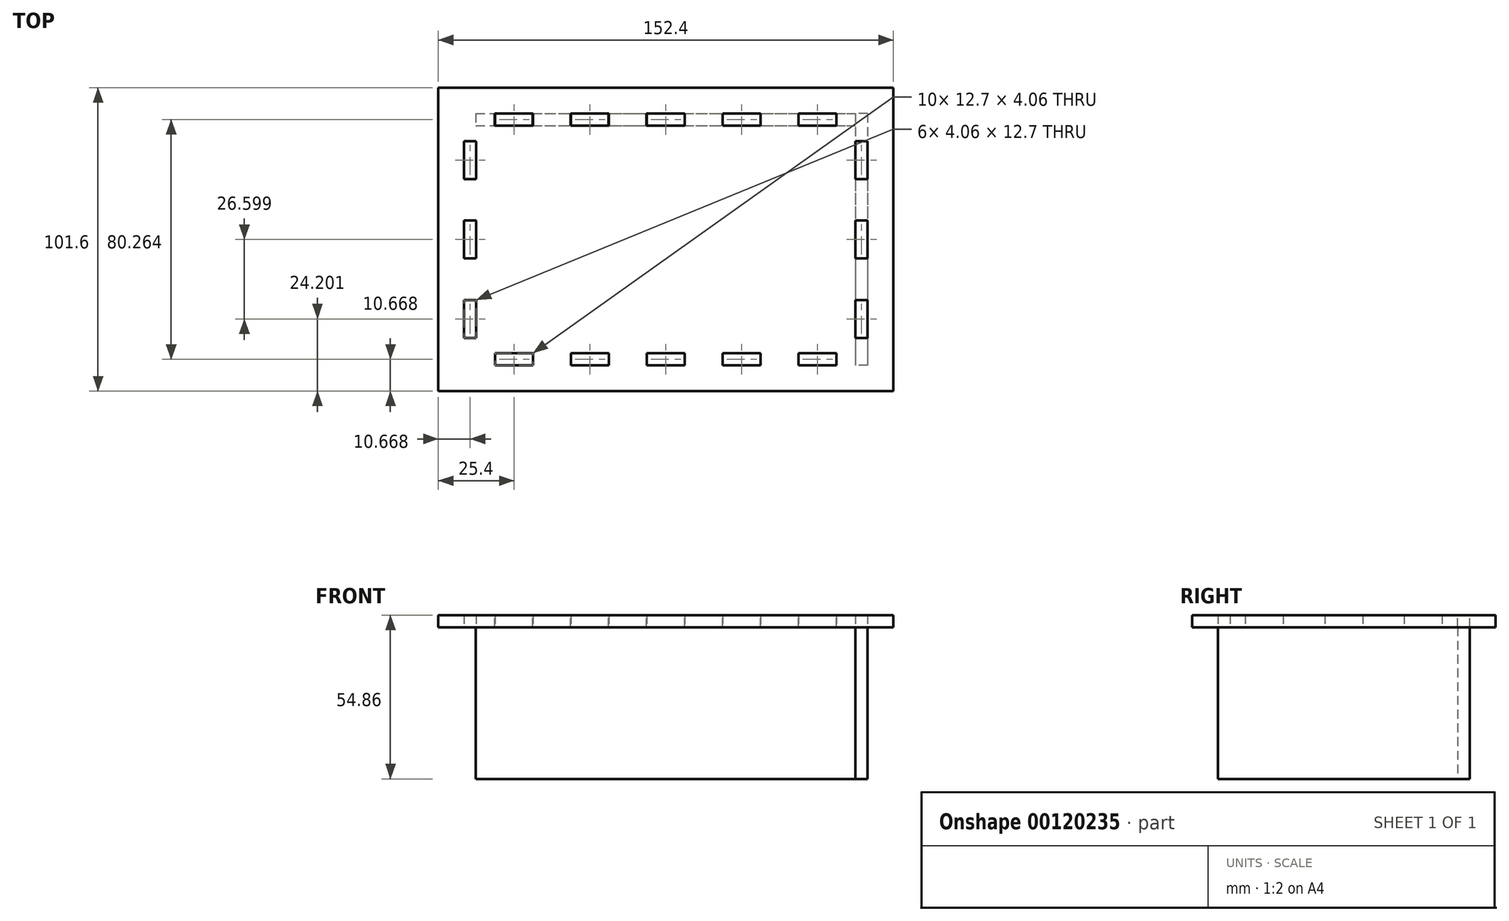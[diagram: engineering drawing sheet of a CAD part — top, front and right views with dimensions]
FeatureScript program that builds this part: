
annotation { "Feature Type Name" : "Feature", "Feature Type Description" : "" }
export const myFeature = defineFeature(function(context is Context, id is Id, definition is map)
    precondition{}
    {
        {
            assignVariable(context, id + "F0", {"name" : "T", "anyValue" : 4.06 * mm});
        }
        {
            var Q0;
            Q0=qCreatedBy(makeId("Top.planeOp"),FACE);
            var sketch = newSketch(context, id + "F1", { "sketchPlane" : qUnion([Q0])});
            skLineSegment(sketch, "E0.bottom", {"start": v(0, 0) * mm, "end": v(152.4, 0) * mm});
            skLineSegment(sketch, "E0.top", {"start": v(0, -101.6) * mm, "end": v(152.4, -101.6) * mm});
            skLineSegment(sketch, "E0.left", {"start": v(0, 0) * mm, "end": v(0, -101.6) * mm});
            skLineSegment(sketch, "E0.right", {"start": v(152.4, 0) * mm, "end": v(152.4, -101.6) * mm});
            skLineSegment(sketch, "E1.bottom", {"start": v(19.05, -8.64) * mm, "end": v(31.75, -8.64) * mm});
            skLineSegment(sketch, "E1.top", {"start": v(19.05, -12.7) * mm, "end": v(31.75, -12.7) * mm});
            skLineSegment(sketch, "E1.left", {"start": v(19.05, -8.64) * mm, "end": v(19.05, -12.7) * mm});
            skLineSegment(sketch, "E1.right", {"start": v(31.75, -8.64) * mm, "end": v(31.75, -12.7) * mm});
            skLineSegment(sketch, "E2.1.0.0", {"start": v(57.15, -8.64) * mm, "end": v(57.15, -12.7) * mm});
            skLineSegment(sketch, "E2.1.0.1", {"start": v(44.45, -8.64) * mm, "end": v(44.45, -12.7) * mm});
            skLineSegment(sketch, "E2.1.0.2", {"start": v(44.45, -12.7) * mm, "end": v(57.15, -12.7) * mm});
            skLineSegment(sketch, "E2.1.0.3", {"start": v(44.45, -8.64) * mm, "end": v(57.15, -8.64) * mm});
            skLineSegment(sketch, "E2.2.0.0", {"start": v(82.55, -8.64) * mm, "end": v(82.55, -12.7) * mm});
            skLineSegment(sketch, "E2.2.0.1", {"start": v(69.85, -8.64) * mm, "end": v(69.85, -12.7) * mm});
            skLineSegment(sketch, "E2.2.0.2", {"start": v(69.85, -12.7) * mm, "end": v(82.55, -12.7) * mm});
            skLineSegment(sketch, "E2.2.0.3", {"start": v(69.85, -8.64) * mm, "end": v(82.55, -8.64) * mm});
            skLineSegment(sketch, "E2.3.0.0", {"start": v(107.95, -8.64) * mm, "end": v(107.95, -12.7) * mm});
            skLineSegment(sketch, "E2.3.0.1", {"start": v(95.25, -8.64) * mm, "end": v(95.25, -12.7) * mm});
            skLineSegment(sketch, "E2.3.0.2", {"start": v(95.25, -12.7) * mm, "end": v(107.95, -12.7) * mm});
            skLineSegment(sketch, "E2.3.0.3", {"start": v(95.25, -8.64) * mm, "end": v(107.95, -8.64) * mm});
            skLineSegment(sketch, "E2.4.0.0", {"start": v(133.35, -8.64) * mm, "end": v(133.35, -12.7) * mm});
            skLineSegment(sketch, "E2.4.0.1", {"start": v(120.65, -8.64) * mm, "end": v(120.65, -12.7) * mm});
            skLineSegment(sketch, "E2.4.0.2", {"start": v(120.65, -12.7) * mm, "end": v(133.35, -12.7) * mm});
            skLineSegment(sketch, "E2.4.0.3", {"start": v(120.65, -8.64) * mm, "end": v(133.35, -8.64) * mm});
            skLineSegment(sketch, "E2.direction1", {"start": v(19.05, -12.7) * mm, "end": v(44.45, -12.7) * mm, "construction": true});
            skLineSegment(sketch, "E3", {"start": v(0, -50.8) * mm, "end": v(152.4, -50.8) * mm, "construction": true});
            skLineSegment(sketch, "E4.MirrorCS", {"start": v(19.05, -88.9) * mm, "end": v(31.75, -88.9) * mm});
            skLineSegment(sketch, "E5.MirrorCS", {"start": v(19.05, -88.9) * mm, "end": v(44.45, -88.9) * mm, "construction": true});
            skLineSegment(sketch, "E6.MirrorCS", {"start": v(95.25, -92.96) * mm, "end": v(107.95, -92.96) * mm});
            skLineSegment(sketch, "E7.MirrorCS", {"start": v(120.65, -92.96) * mm, "end": v(120.65, -88.9) * mm});
            skLineSegment(sketch, "E8.MirrorCS", {"start": v(69.85, -92.96) * mm, "end": v(69.85, -88.9) * mm});
            skLineSegment(sketch, "E9.MirrorCS", {"start": v(95.25, -92.96) * mm, "end": v(95.25, -88.9) * mm});
            skLineSegment(sketch, "E10.MirrorCS", {"start": v(69.85, -88.9) * mm, "end": v(82.55, -88.9) * mm});
            skLineSegment(sketch, "E11.MirrorCS", {"start": v(69.85, -92.96) * mm, "end": v(82.55, -92.96) * mm});
            skLineSegment(sketch, "E12.MirrorCS", {"start": v(120.65, -88.9) * mm, "end": v(133.35, -88.9) * mm});
            skLineSegment(sketch, "E13.MirrorCS", {"start": v(95.25, -88.9) * mm, "end": v(107.95, -88.9) * mm});
            skLineSegment(sketch, "E14.MirrorCS", {"start": v(19.05, -92.96) * mm, "end": v(31.75, -92.96) * mm});
            skLineSegment(sketch, "E15.MirrorCS", {"start": v(19.05, -92.96) * mm, "end": v(19.05, -88.9) * mm});
            skLineSegment(sketch, "E16.MirrorCS", {"start": v(133.35, -92.96) * mm, "end": v(133.35, -88.9) * mm});
            skLineSegment(sketch, "E17.MirrorCS", {"start": v(31.75, -92.96) * mm, "end": v(31.75, -88.9) * mm});
            skLineSegment(sketch, "E18.MirrorCS", {"start": v(107.95, -92.96) * mm, "end": v(107.95, -88.9) * mm});
            skLineSegment(sketch, "E19.MirrorCS", {"start": v(57.15, -92.96) * mm, "end": v(57.15, -88.9) * mm});
            skLineSegment(sketch, "E20.MirrorCS", {"start": v(44.45, -92.96) * mm, "end": v(44.45, -88.9) * mm});
            skLineSegment(sketch, "E21.MirrorCS", {"start": v(44.45, -88.9) * mm, "end": v(57.15, -88.9) * mm});
            skLineSegment(sketch, "E22.MirrorCS", {"start": v(44.45, -92.96) * mm, "end": v(57.15, -92.96) * mm});
            skLineSegment(sketch, "E23.MirrorCS", {"start": v(82.55, -92.96) * mm, "end": v(82.55, -88.9) * mm});
            skLineSegment(sketch, "E24.MirrorCS", {"start": v(120.65, -92.96) * mm, "end": v(133.35, -92.96) * mm});
            skLineSegment(sketch, "E25.bottom", {"start": v(139.7, -17.85) * mm, "end": v(143.76, -17.85) * mm});
            skLineSegment(sketch, "E25.top", {"start": v(139.7, -30.55) * mm, "end": v(143.76, -30.55) * mm});
            skLineSegment(sketch, "E25.left", {"start": v(139.7, -17.85) * mm, "end": v(139.7, -30.55) * mm});
            skLineSegment(sketch, "E25.right", {"start": v(143.76, -17.85) * mm, "end": v(143.76, -30.55) * mm});
            skLineSegment(sketch, "E26.1.0.0", {"start": v(143.76, -44.45) * mm, "end": v(143.76, -57.15) * mm});
            skLineSegment(sketch, "E26.1.0.1", {"start": v(139.7, -44.45) * mm, "end": v(139.7, -57.15) * mm});
            skLineSegment(sketch, "E26.1.0.2", {"start": v(139.7, -44.45) * mm, "end": v(143.76, -44.45) * mm});
            skLineSegment(sketch, "E26.1.0.3", {"start": v(139.7, -57.15) * mm, "end": v(143.76, -57.15) * mm});
            skLineSegment(sketch, "E26.2.0.0", {"start": v(143.76, -71.05) * mm, "end": v(143.76, -83.75) * mm});
            skLineSegment(sketch, "E26.2.0.1", {"start": v(139.7, -71.05) * mm, "end": v(139.7, -83.75) * mm});
            skLineSegment(sketch, "E26.2.0.2", {"start": v(139.7, -71.05) * mm, "end": v(143.76, -71.05) * mm});
            skLineSegment(sketch, "E26.2.0.3", {"start": v(139.7, -83.75) * mm, "end": v(143.76, -83.75) * mm});
            skLineSegment(sketch, "E26.direction1", {"start": v(139.7, -30.55) * mm, "end": v(139.7, -57.15) * mm, "construction": true});
            skPoint(sketch, "E27", {"position": v(143.76, -50.8) * mm});
            skLineSegment(sketch, "E28", {"start": v(76.2, 0) * mm, "end": v(76.2, -101.6) * mm, "construction": true});
            skLineSegment(sketch, "E29.MirrorCS", {"start": v(12.7, -44.45) * mm, "end": v(12.7, -57.15) * mm});
            skLineSegment(sketch, "E30.MirrorCS", {"start": v(12.7, -17.85) * mm, "end": v(8.64, -17.85) * mm});
            skLineSegment(sketch, "E31.MirrorCS", {"start": v(12.7, -57.15) * mm, "end": v(8.64, -57.15) * mm});
            skLineSegment(sketch, "E32.MirrorCS", {"start": v(12.7, -71.05) * mm, "end": v(8.64, -71.05) * mm});
            skLineSegment(sketch, "E33.MirrorCS", {"start": v(12.7, -71.05) * mm, "end": v(12.7, -83.75) * mm});
            skLineSegment(sketch, "E34.MirrorCS", {"start": v(12.7, -44.45) * mm, "end": v(8.64, -44.45) * mm});
            skLineSegment(sketch, "E35.MirrorCS", {"start": v(12.7, -30.55) * mm, "end": v(12.7, -57.15) * mm, "construction": true});
            skLineSegment(sketch, "E36.MirrorCS", {"start": v(8.64, -71.05) * mm, "end": v(8.64, -83.75) * mm});
            skLineSegment(sketch, "E37.MirrorCS", {"start": v(12.7, -17.85) * mm, "end": v(12.7, -30.55) * mm});
            skPoint(sketch, "E38.MirrorP", {"position": v(8.64, -50.8) * mm});
            skLineSegment(sketch, "E39.MirrorCS", {"start": v(8.64, -44.45) * mm, "end": v(8.64, -57.15) * mm});
            skLineSegment(sketch, "E40.MirrorCS", {"start": v(12.7, -30.55) * mm, "end": v(8.64, -30.55) * mm});
            skLineSegment(sketch, "E41.MirrorCS", {"start": v(8.64, -17.85) * mm, "end": v(8.64, -30.55) * mm});
            skLineSegment(sketch, "E42.MirrorCS", {"start": v(12.7, -83.75) * mm, "end": v(8.64, -83.75) * mm});
            skSolve(sketch);
        }
        {
            var Q0;
            Q0=makeQuery(id+"F1.imprint","IMPRINT",FACE,{"disambiguationData":[TD([[makeQuery(id+"F1.imprint","IMPRINT",EDGE,{"derivedFrom":sQuery(id+"F1.wireOp",EDGE,"E0.bottom")}),-1.0]])]});
            extrude(context, id + "F2", {"entities" : qUnion([Q0]), "depth" : getVariable(context, 'T')});
        }
        {
            var Q0;
            Q0=makeQuery(id+"F2.opExtrude","SWEPT_FACE",FACE,{"disambiguationData":[OSD([sQuery(id+"F1.wireOp",EDGE,"E2.2.0.2")])]});
            var sketch = newSketch(context, id + "F3", { "sketchPlane" : qUnion([Q0])});
            skLineSegment(sketch, "E43.bottom", {"start": v(-12.6, 0) * mm, "end": v(-139.6, 0) * mm});
            skLineSegment(sketch, "E43.top", {"start": v(-12.6, -50.8) * mm, "end": v(-139.6, -50.8) * mm});
            skLineSegment(sketch, "E43.left", {"start": v(-12.6, 0) * mm, "end": v(-12.6, -50.8) * mm});
            skLineSegment(sketch, "E43.right", {"start": v(-139.6, 0) * mm, "end": v(-139.6, -50.8) * mm});
            skLineSegment(sketch, "E44.bottom", {"start": v(-18.96, 0) * mm, "end": v(-31.66, 0) * mm});
            skLineSegment(sketch, "E44.top", {"start": v(-18.96, 4.06) * mm, "end": v(-31.66, 4.06) * mm});
            skLineSegment(sketch, "E44.left", {"start": v(-18.96, 0) * mm, "end": v(-18.96, 4.06) * mm});
            skLineSegment(sketch, "E44.right", {"start": v(-31.66, 0) * mm, "end": v(-31.66, 4.06) * mm});
            skLineSegment(sketch, "E45.1.0.0", {"start": v(-57.06, 0) * mm, "end": v(-57.06, 4.06) * mm});
            skLineSegment(sketch, "E45.1.0.1", {"start": v(-44.36, 0) * mm, "end": v(-57.06, 0) * mm});
            skLineSegment(sketch, "E45.1.0.2", {"start": v(-44.36, 4.06) * mm, "end": v(-57.06, 4.06) * mm});
            skLineSegment(sketch, "E45.1.0.3", {"start": v(-44.36, 0) * mm, "end": v(-44.36, 4.06) * mm});
            skLineSegment(sketch, "E45.2.0.0", {"start": v(-82.46, 0) * mm, "end": v(-82.46, 4.06) * mm});
            skLineSegment(sketch, "E45.2.0.1", {"start": v(-69.76, 0) * mm, "end": v(-82.46, 0) * mm});
            skLineSegment(sketch, "E45.2.0.2", {"start": v(-69.76, 4.06) * mm, "end": v(-82.46, 4.06) * mm});
            skLineSegment(sketch, "E45.2.0.3", {"start": v(-69.76, 0) * mm, "end": v(-69.76, 4.06) * mm});
            skLineSegment(sketch, "E45.3.0.0", {"start": v(-107.86, 0) * mm, "end": v(-107.86, 4.06) * mm});
            skLineSegment(sketch, "E45.3.0.1", {"start": v(-95.16, 0) * mm, "end": v(-107.86, 0) * mm});
            skLineSegment(sketch, "E45.3.0.2", {"start": v(-95.16, 4.06) * mm, "end": v(-107.86, 4.06) * mm});
            skLineSegment(sketch, "E45.3.0.3", {"start": v(-95.16, 0) * mm, "end": v(-95.16, 4.06) * mm});
            skLineSegment(sketch, "E45.4.0.0", {"start": v(-133.26, 0) * mm, "end": v(-133.26, 4.06) * mm});
            skLineSegment(sketch, "E45.4.0.1", {"start": v(-120.56, 0) * mm, "end": v(-133.26, 0) * mm});
            skLineSegment(sketch, "E45.4.0.2", {"start": v(-120.56, 4.06) * mm, "end": v(-133.26, 4.06) * mm});
            skLineSegment(sketch, "E45.4.0.3", {"start": v(-120.56, 0) * mm, "end": v(-120.56, 4.06) * mm});
            skLineSegment(sketch, "E45.direction1", {"start": v(-31.66, 0) * mm, "end": v(-57.06, 0) * mm, "construction": true});
            skSolve(sketch);
        }
        {
            var Q0;
            Q0 = qSketchRegion(id + "F3", true);
            extrude(context, id + "F4", {"entities" : qUnion([Q0]), "depth" : getVariable(context, 'T')});
        }
        {
            var Q0;
            Q0=makeQuery(id+"F2.opExtrude","SWEPT_FACE",FACE,{"disambiguationData":[OSD([sQuery(id+"F1.wireOp",EDGE,"E26.1.0.1")])]});
            var sketch = newSketch(context, id + "F5", { "sketchPlane" : qUnion([Q0])});
            skLineSegment(sketch, "E46.bottom", {"start": v(-8.64, 0) * mm, "end": v(-92.96, 0) * mm});
            skLineSegment(sketch, "E46.top", {"start": v(-8.64, -50.8) * mm, "end": v(-92.96, -50.8) * mm});
            skLineSegment(sketch, "E46.left", {"start": v(-8.64, 0) * mm, "end": v(-8.64, -50.8) * mm});
            skLineSegment(sketch, "E46.right", {"start": v(-92.96, 0) * mm, "end": v(-92.96, -50.8) * mm});
            skLineSegment(sketch, "E47", {"start": v(-50.8, 0) * mm, "end": v(-50.8, -65.37) * mm, "construction": true});
            skPoint(sketch, "E47.endSnap0", {"position": v(-50.8, 0) * mm});
            skLineSegment(sketch, "E48.bottom", {"start": v(-83.75, 0) * mm, "end": v(-71.05, 0) * mm});
            skLineSegment(sketch, "E48.top", {"start": v(-83.75, 4.06) * mm, "end": v(-71.05, 4.06) * mm});
            skLineSegment(sketch, "E48.left", {"start": v(-83.75, 0) * mm, "end": v(-83.75, 4.06) * mm});
            skLineSegment(sketch, "E48.right", {"start": v(-71.05, 0) * mm, "end": v(-71.05, 4.06) * mm});
            skLineSegment(sketch, "E49.bottom", {"start": v(-57.15, 4.06) * mm, "end": v(-44.45, 4.06) * mm});
            skLineSegment(sketch, "E49.top", {"start": v(-57.15, 0) * mm, "end": v(-44.45, 0) * mm});
            skLineSegment(sketch, "E49.left", {"start": v(-57.15, 4.06) * mm, "end": v(-57.15, 0) * mm});
            skLineSegment(sketch, "E49.right", {"start": v(-44.45, 4.06) * mm, "end": v(-44.45, 0) * mm});
            skLineSegment(sketch, "E50.bottom", {"start": v(-30.55, 0) * mm, "end": v(-17.85, 0) * mm});
            skLineSegment(sketch, "E50.top", {"start": v(-30.55, 4.06) * mm, "end": v(-17.85, 4.06) * mm});
            skLineSegment(sketch, "E50.left", {"start": v(-30.55, 0) * mm, "end": v(-30.55, 4.06) * mm});
            skLineSegment(sketch, "E50.right", {"start": v(-17.85, 0) * mm, "end": v(-17.85, 4.06) * mm});
            skSolve(sketch);
        }
        {
            var Q0;
            Q0=makeQuery(id+"F5.imprint","IMPRINT",FACE,{"disambiguationData":[TD([[makeQuery(id+"F5.imprint","IMPRINT",EDGE,{"derivedFrom":sQuery(id+"F5.wireOp",EDGE,"E49.bottom")}),1.0]])]});
            var Q1;
            Q1=makeQuery(id+"F5.imprint","IMPRINT",FACE,{"disambiguationData":[TD([[makeQuery(id+"F5.imprint","IMPRINT",EDGE,{"derivedFrom":sQuery(id+"F5.wireOp",EDGE,"E50.bottom")}),1.0]])]});
            var Q2;
            Q2=makeQuery(id+"F5.imprint","IMPRINT",FACE,{"disambiguationData":[TD([[makeQuery(id+"F5.imprint","IMPRINT",EDGE,{"derivedFrom":sQuery(id+"F5.wireOp",EDGE,"E48.bottom")}),1.0]])]});
            var Q3;
            Q3=makeQuery(id+"F5.imprint","IMPRINT",FACE,{"disambiguationData":[TD([[makeQuery(id+"F5.imprint","IMPRINT",EDGE,{"derivedFrom":sQuery(id+"F5.wireOp",EDGE,"E46.top")}),-1.0]])]});
            extrude(context, id + "F6", {"entities" : qUnion([Q0, Q1, Q2, Q3]), "depth" : getVariable(context, 'T')});
        }
    });
